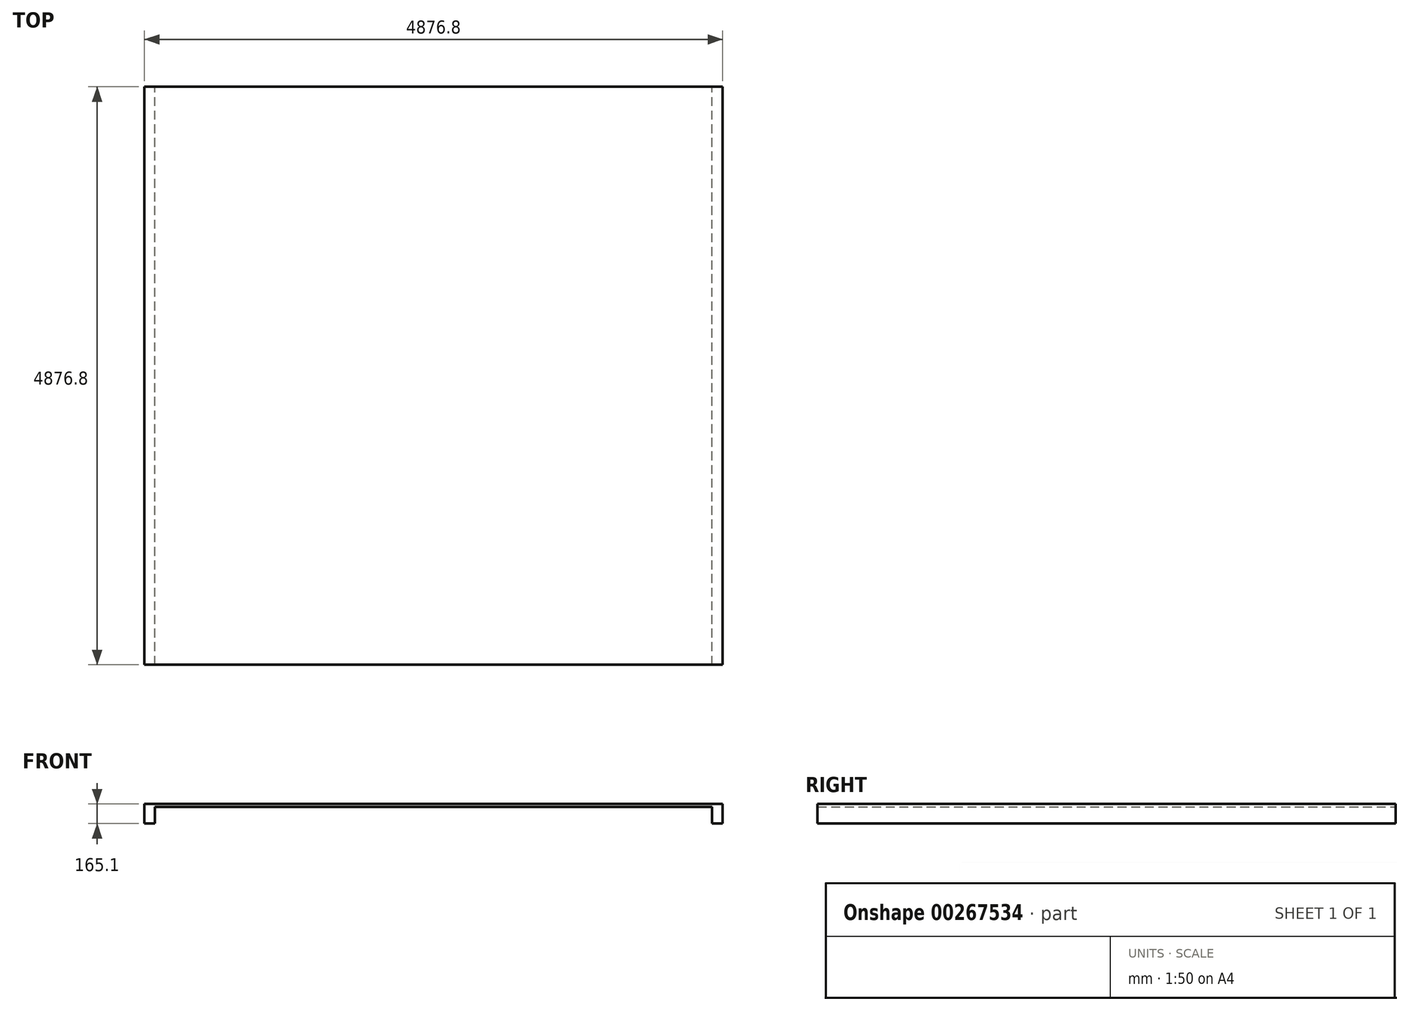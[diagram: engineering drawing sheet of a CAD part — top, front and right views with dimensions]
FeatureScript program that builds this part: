
annotation { "Feature Type Name" : "Feature", "Feature Type Description" : "" }
export const myFeature = defineFeature(function(context is Context, id is Id, definition is map)
    precondition{}
    {
        {
            var Q0;
            Q0=qCreatedBy(makeId("Front.planeOp"),FACE);
            var sketch = newSketch(context, id + "F0", { "sketchPlane" : qUnion([Q0])});
            skLineSegment(sketch, "E0", {"start": v(-2438.4, 0) * mm, "end": v(2438.4, 0) * mm});
            skLineSegment(sketch, "E1", {"start": v(-2438.4, 0) * mm, "end": v(-2438.4, 25.4) * mm});
            skLineSegment(sketch, "E2", {"start": v(-2438.4, 25.4) * mm, "end": v(2438.4, 25.4) * mm});
            skLineSegment(sketch, "E3", {"start": v(2438.4, 25.4) * mm, "end": v(2438.4, 0) * mm});
            skLineSegment(sketch, "E4.bottom", {"start": v(-2438.4, 0) * mm, "end": v(-2349.5, 0) * mm});
            skLineSegment(sketch, "E4.top", {"start": v(-2438.4, -139.7) * mm, "end": v(-2349.5, -139.7) * mm});
            skLineSegment(sketch, "E4.left", {"start": v(-2438.4, 0) * mm, "end": v(-2438.4, -139.7) * mm});
            skLineSegment(sketch, "E4.right", {"start": v(-2349.5, 0) * mm, "end": v(-2349.5, -139.7) * mm});
            skLineSegment(sketch, "E5.bottom", {"start": v(2438.4, 0) * mm, "end": v(2349.5, 0) * mm});
            skLineSegment(sketch, "E5.top", {"start": v(2438.4, -139.7) * mm, "end": v(2349.5, -139.7) * mm});
            skLineSegment(sketch, "E5.left", {"start": v(2438.4, 0) * mm, "end": v(2438.4, -139.7) * mm});
            skLineSegment(sketch, "E5.right", {"start": v(2349.5, 0) * mm, "end": v(2349.5, -139.7) * mm});
            skSolve(sketch);
        }
        {
            var Q0;
            Q0 = qSketchRegion(id + "F0", true);
            extrude(context, id + "F1", {"entities" : qUnion([Q0]), "endBound" : BoundingType.SYMMETRIC, "depth" : 4876.8 * mm});
        }
    });
